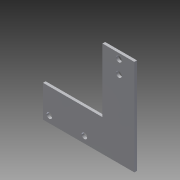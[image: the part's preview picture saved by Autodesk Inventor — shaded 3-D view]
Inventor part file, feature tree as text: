
AUTODESK INVENTOR PART (.ipt)
format: ipt  version: 2013 (Build 170138000, 138)  size: 147,456 bytes
history: native  units: in
note: dims shown in document units (in); Inventor stores cm internally (conversion verified against a paired STEP export)
features: sketch x6, other x5, reference x4, extrude x2, sheet_metal_op x1
ambient origin geometry x8: Origin, YZ Plane, XZ Plane, XY Plane, X Axis, Y Axis, Z Axis, Center Point
bodies: Solid1 (feature_tree)
feature tree (18):
  sheet_metal_op  "Face1"
  extrude  "Extrusion1"  Depth=1.5in
  extrude  "Extrusion2"  Depth=1.181in
  sketch  "Sketch1"  dims[d1=2.244in d2=1.5in]
  other  "Plate1"
  sketch  "Sketch8"  dims[d3=0.295in d4=1.181in]
  reference  "Reference1"
  reference  "Reference2"
  sketch  "Sketch10"  dims[d5=0.295in]
  sketch  "Sketch13"  dims[d8=0.125in]
  sketch  "Sketch14"  dims[d19=0.125in]
  reference  "Reference7"
  reference  "Reference8"
  sketch  "Sketch15"  dims[d20=0.0in d21=2.053in d22=0.0in d27=3.0in d28=0.0in d29=0.125in d30=0.0in d31=1.5in d32=0.125in d33=0.0in]
  other  "Cut1"
  other  "Cut4"
  other  "Cut5"
  other  "Definition1"
